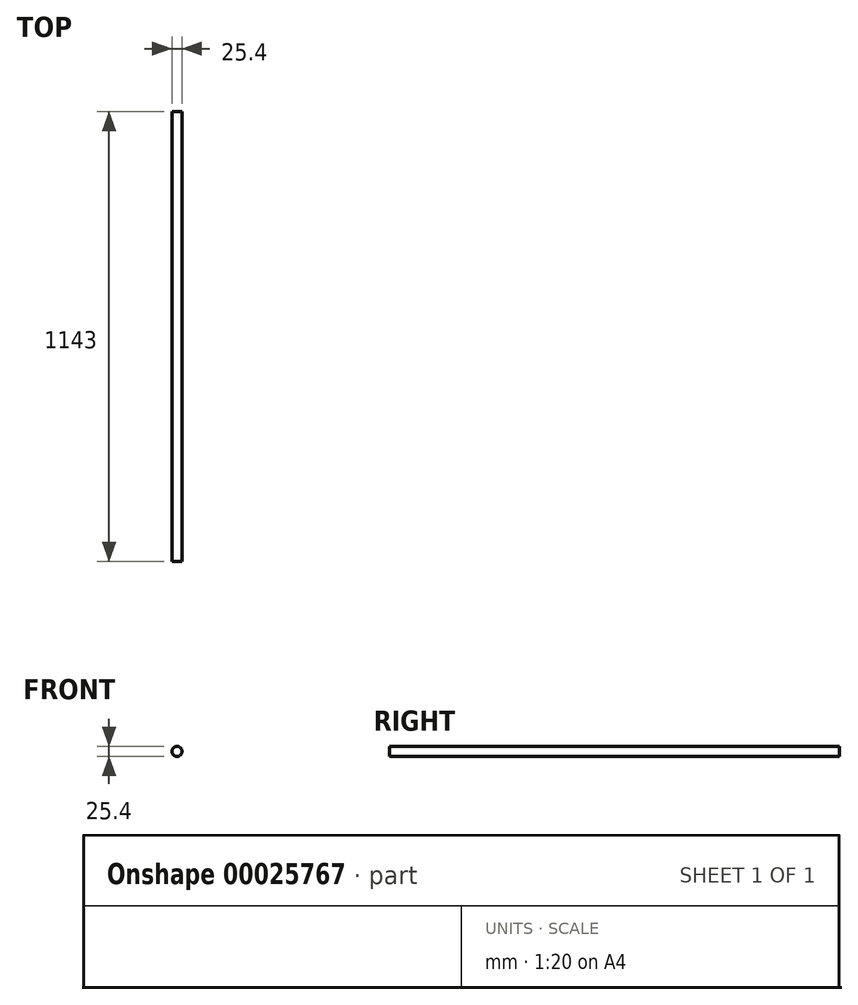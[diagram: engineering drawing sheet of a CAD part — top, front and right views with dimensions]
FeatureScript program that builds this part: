
annotation { "Feature Type Name" : "Feature", "Feature Type Description" : "" }
export const myFeature = defineFeature(function(context is Context, id is Id, definition is map)
    precondition{}
    {
        {
            var Q0;
            Q0=qCreatedBy(makeId("Front.planeOp"),FACE);
            var sketch = newSketch(context, id + "F0", { "sketchPlane" : qUnion([Q0])});
            skCircle(sketch, "E0", {"center": v(0, 0) * mm, "radius": 12.7 * mm});
            skSolve(sketch);
        }
        {
            var Q0;
            Q0 = qSketchRegion(id + "F0", true);
            extrude(context, id + "F1", {"entities" : qUnion([Q0]), "depth" : 1143 * mm});
        }
    });
